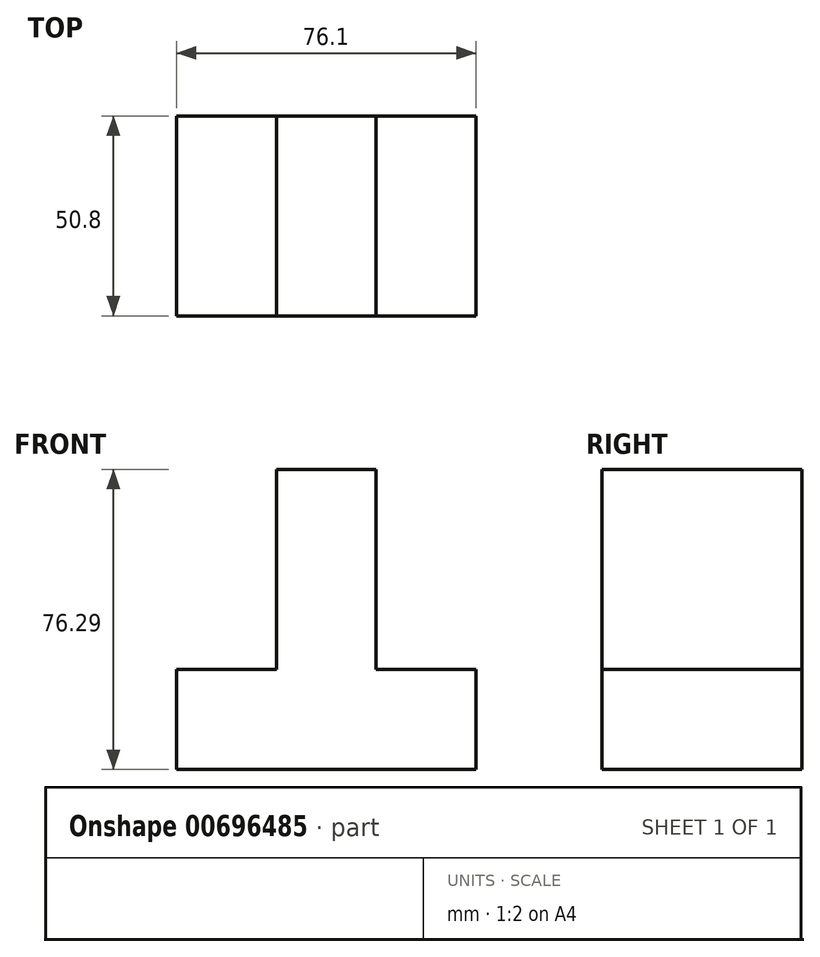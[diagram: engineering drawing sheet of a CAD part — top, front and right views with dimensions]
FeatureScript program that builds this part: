
annotation { "Feature Type Name" : "Feature", "Feature Type Description" : "" }
export const myFeature = defineFeature(function(context is Context, id is Id, definition is map)
    precondition{}
    {
        {
            var Q0;
            Q0=qCreatedBy(makeId("Front.planeOp"),FACE);
            var sketch = newSketch(context, id + "F0", { "sketchPlane" : qUnion([Q0])});
            skLineSegment(sketch, "E0", {"start": v(0, 0) * mm, "end": v(0, 25.5) * mm});
            skLineSegment(sketch, "E1", {"start": v(0, 25.5) * mm, "end": v(25.5, 25.5) * mm});
            skLineSegment(sketch, "E2", {"start": v(25.5, 25.5) * mm, "end": v(25.5, 76.29) * mm});
            skLineSegment(sketch, "E3", {"start": v(76.1, 0) * mm, "end": v(0, 0) * mm});
            skLineSegment(sketch, "E4", {"start": v(76.1, 0) * mm, "end": v(76.1, 25.5) * mm});
            skLineSegment(sketch, "E5", {"start": v(76.1, 25.5) * mm, "end": v(50.7, 25.5) * mm});
            skLineSegment(sketch, "E6", {"start": v(50.7, 76.29) * mm, "end": v(50.7, 25.5) * mm});
            skPoint(sketch, "E7.start.orphan", {"position": v(27.21, 76.29) * mm});
            skLineSegment(sketch, "E8", {"start": v(25.5, 76.29) * mm, "end": v(50.7, 76.29) * mm});
            skSolve(sketch);
        }
        {
            var Q0;
            Q0=makeQuery(id+"F0.imprint","IMPRINT",FACE,{"disambiguationData":[TD([[makeQuery(id+"F0.imprint","IMPRINT",EDGE,{"derivedFrom":sQuery(id+"F0.wireOp",EDGE,"E0")}),-1.0]])]});
            extrude(context, id + "F1", {"entities" : qUnion([Q0]), "depth" : 50.8 * mm, "offsetDistance" : 25.4 * mm});
        }
    });
